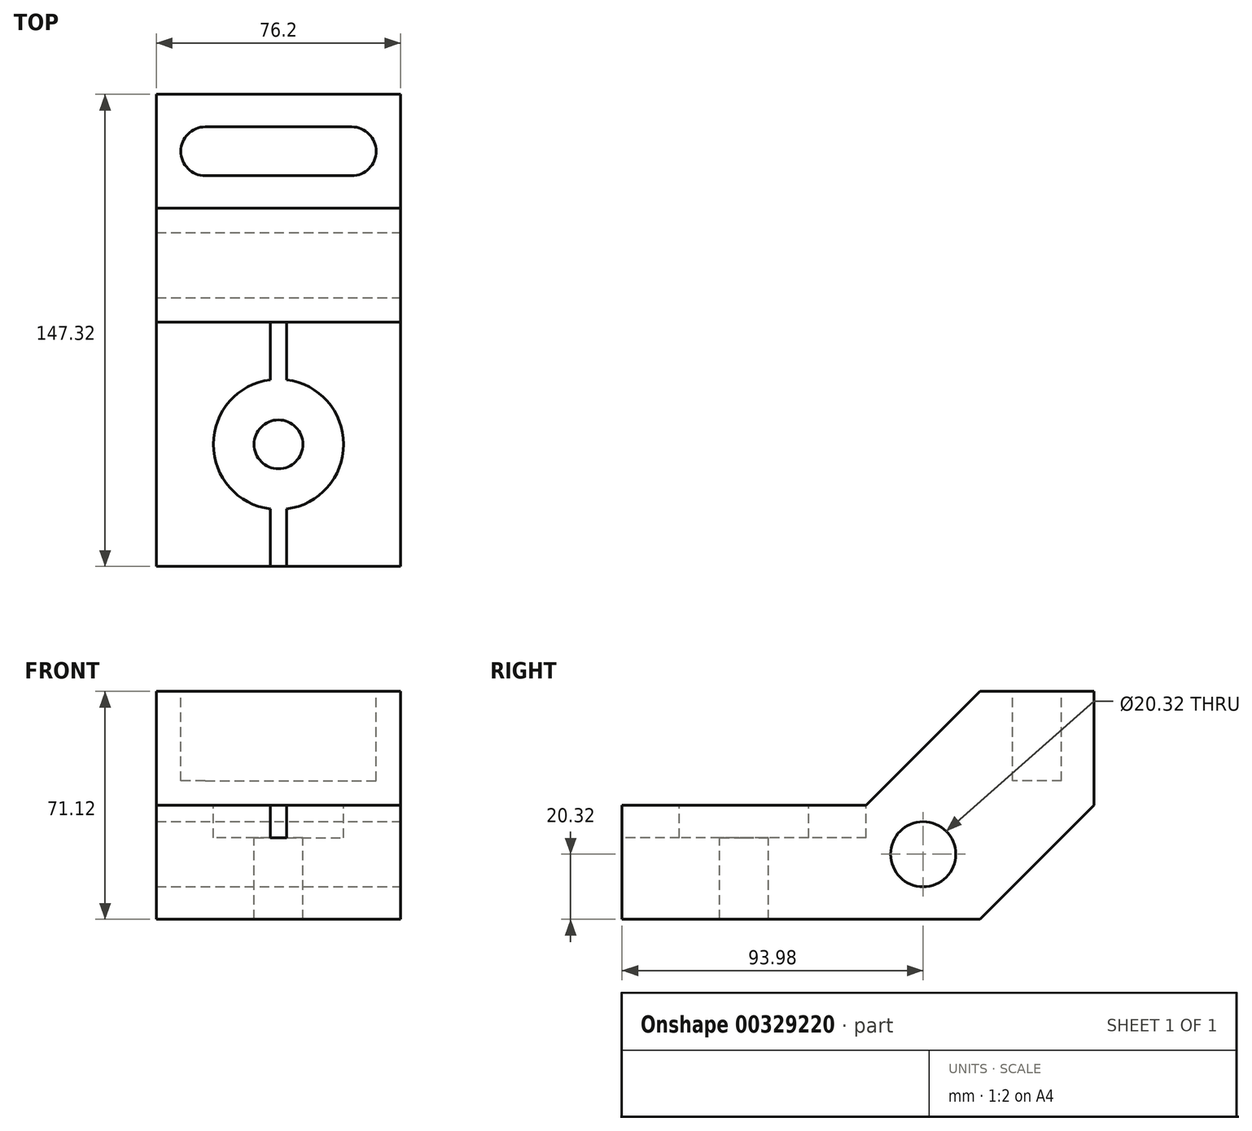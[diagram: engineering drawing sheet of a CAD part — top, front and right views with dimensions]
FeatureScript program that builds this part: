
annotation { "Feature Type Name" : "Feature", "Feature Type Description" : "" }
export const myFeature = defineFeature(function(context is Context, id is Id, definition is map)
    precondition{}
    {
        {
            var Q0;
            Q0=qCreatedBy(makeId("Right.planeOp"),FACE);
            var sketch = newSketch(context, id + "F0", { "sketchPlane" : qUnion([Q0])});
            skLineSegment(sketch, "E0", {"start": v(0, 0) * mm, "end": v(0, 35.56) * mm});
            skLineSegment(sketch, "E1", {"start": v(0, 35.56) * mm, "end": v(76.2, 35.56) * mm});
            skLineSegment(sketch, "E2", {"start": v(76.2, 35.56) * mm, "end": v(111.76, 71.12) * mm});
            skLineSegment(sketch, "E3", {"start": v(111.76, 71.12) * mm, "end": v(147.32, 71.12) * mm});
            skLineSegment(sketch, "E4", {"start": v(147.32, 71.12) * mm, "end": v(147.32, 35.56) * mm});
            skLineSegment(sketch, "E5", {"start": v(147.32, 35.56) * mm, "end": v(111.76, 0) * mm});
            skLineSegment(sketch, "E6", {"start": v(111.76, 0) * mm, "end": v(0, 0) * mm});
            skSolve(sketch);
        }
        {
            var Q0;
            Q0 = qSketchRegion(id + "F0", true);
            extrude(context, id + "F1", {"entities" : qUnion([Q0]), "depth" : 76.2 * mm});
        }
        {
            var Q0;
            Q0=makeQuery(id+"F1.opExtrude","CAP_FACE",FACE,{"disambiguationData":[OSD([sQuery(id+"F0.wireOp",EDGE,"E0"),sQuery(id+"F0.wireOp",EDGE,"E1"),sQuery(id+"F0.wireOp",EDGE,"E2"),sQuery(id+"F0.wireOp",EDGE,"E3"),sQuery(id+"F0.wireOp",EDGE,"E4"),sQuery(id+"F0.wireOp",EDGE,"E5"),sQuery(id+"F0.wireOp",EDGE,"E6")])],"isStart":false});
            var sketch = newSketch(context, id + "F2", { "sketchPlane" : qUnion([Q0])});
            skCircle(sketch, "E7", {"center": v(93.98, 20.32) * mm, "radius": 10.16 * mm});
            skSolve(sketch);
        }
        {
            var Q0;
            Q0=makeQuery(id+"F1.opExtrude","SWEPT_FACE",FACE,{"disambiguationData":[OSD([sQuery(id+"F0.wireOp",EDGE,"E1")])]});
            var sketch = newSketch(context, id + "F3", { "sketchPlane" : qUnion([Q0])});
            skArc(sketch, "E8", {"start": v(35.56, 58.26) * mm, "mid": v(17.78, 38.1) * mm, "end": v(35.56, 17.94) * mm});
            skLineSegment(sketch, "E9", {"start": v(38.1, 76.2) * mm, "end": v(38.1, 0) * mm, "construction": true});
            skLineSegment(sketch, "E10", {"start": v(35.56, 76.2) * mm, "end": v(35.56, 58.26) * mm});
            skLineSegment(sketch, "E11", {"start": v(40.64, 76.2) * mm, "end": v(40.64, 58.26) * mm});
            skArc(sketch, "E12.trimOffspring", {"start": v(40.64, 17.94) * mm, "mid": v(58.42, 38.1) * mm, "end": v(40.64, 58.26) * mm});
            skLineSegment(sketch, "E13.trimOffspring", {"start": v(35.56, 17.94) * mm, "end": v(35.56, 0) * mm});
            skLineSegment(sketch, "E14.trimOffspring", {"start": v(40.64, 17.94) * mm, "end": v(40.64, 0) * mm});
            skLineSegment(sketch, "E15", {"start": v(40.64, 0) * mm, "end": v(35.56, 0) * mm});
            skLineSegment(sketch, "E16", {"start": v(40.64, 76.2) * mm, "end": v(35.56, 76.2) * mm});
            skSolve(sketch);
        }
        {
            var Q0;
            Q0 = qSketchRegion(id + "F3", true);
            extrude(context, id + "F4", {"entities" : qUnion([Q0]), "operationType" : NewBodyOperationType.REMOVE, "oppositeDirection" : true, "depth" : 10.16 * mm});
        }
        {
            var Q0;
            Q0=makeQuery(id+"F1.opExtrude","SWEPT_FACE",FACE,{"disambiguationData":[OSD([sQuery(id+"F0.wireOp",EDGE,"E3")])]});
            var sketch = newSketch(context, id + "F5", { "sketchPlane" : qUnion([Q0])});
            skArc(sketch, "E17", {"start": v(15.24, 137.16) * mm, "mid": v(7.62, 129.54) * mm, "end": v(15.24, 121.92) * mm});
            skArc(sketch, "E18", {"start": v(60.96, 121.92) * mm, "mid": v(68.58, 129.54) * mm, "end": v(60.96, 137.16) * mm});
            skLineSegment(sketch, "E19", {"start": v(15.24, 137.16) * mm, "end": v(60.96, 137.16) * mm});
            skLineSegment(sketch, "E20", {"start": v(60.96, 121.92) * mm, "end": v(15.24, 121.92) * mm});
            skSolve(sketch);
        }
        {
            var Q0;
            Q0=makeQuery(id+"F4.boolean.opBoolean","COPY",FACE,{"derivedFrom":makeQuery(id+"F4.opExtrude","CAP_FACE",FACE,{"disambiguationData":[OSD([sQuery(id+"F3.wireOp",EDGE,"E8"),sQuery(id+"F3.wireOp",EDGE,"E10"),sQuery(id+"F3.wireOp",EDGE,"E11"),sQuery(id+"F3.wireOp",EDGE,"E12.trimOffspring"),sQuery(id+"F3.wireOp",EDGE,"E13.trimOffspring"),sQuery(id+"F3.wireOp",EDGE,"E14.trimOffspring"),sQuery(id+"F3.wireOp",EDGE,"E15"),sQuery(id+"F3.wireOp",EDGE,"E16")])],"isStart":false})});
            var sketch = newSketch(context, id + "F6", { "sketchPlane" : qUnion([Q0])});
            skCircle(sketch, "E21", {"center": v(38.1, 38.1) * mm, "radius": 7.62 * mm});
            skSolve(sketch);
        }
        {
            var Q0;
            Q0 = qSketchRegion(id + "F6", true);
            extrude(context, id + "F7", {"entities" : qUnion([Q0]), "operationType" : NewBodyOperationType.REMOVE, "endBound" : BoundingType.THROUGH_ALL, "oppositeDirection" : true, "depth" : 25.4 * mm});
        }
        {
            var Q0;
            Q0=makeQuery(id+"F2.imprint","IMPRINT",FACE,{"disambiguationData":[TD([[makeQuery(id+"F2.imprint","IMPRINT",EDGE,{"derivedFrom":sQuery(id+"F2.wireOp",EDGE,"E7")}),1.0]])]});
            extrude(context, id + "F8", {"entities" : qUnion([Q0]), "operationType" : NewBodyOperationType.REMOVE, "endBound" : BoundingType.THROUGH_ALL, "oppositeDirection" : true, "depth" : 25.4 * mm});
        }
        {
            var Q0;
            Q0=makeQuery(id+"F5.imprint","IMPRINT",FACE,{"disambiguationData":[TD([[makeQuery(id+"F5.imprint","IMPRINT",EDGE,{"derivedFrom":sQuery(id+"F5.wireOp",EDGE,"E17")}),1.0]])]});
            extrude(context, id + "F9", {"entities" : qUnion([Q0]), "operationType" : NewBodyOperationType.REMOVE, "oppositeDirection" : true, "depth" : 27.94 * mm});
        }
    });
